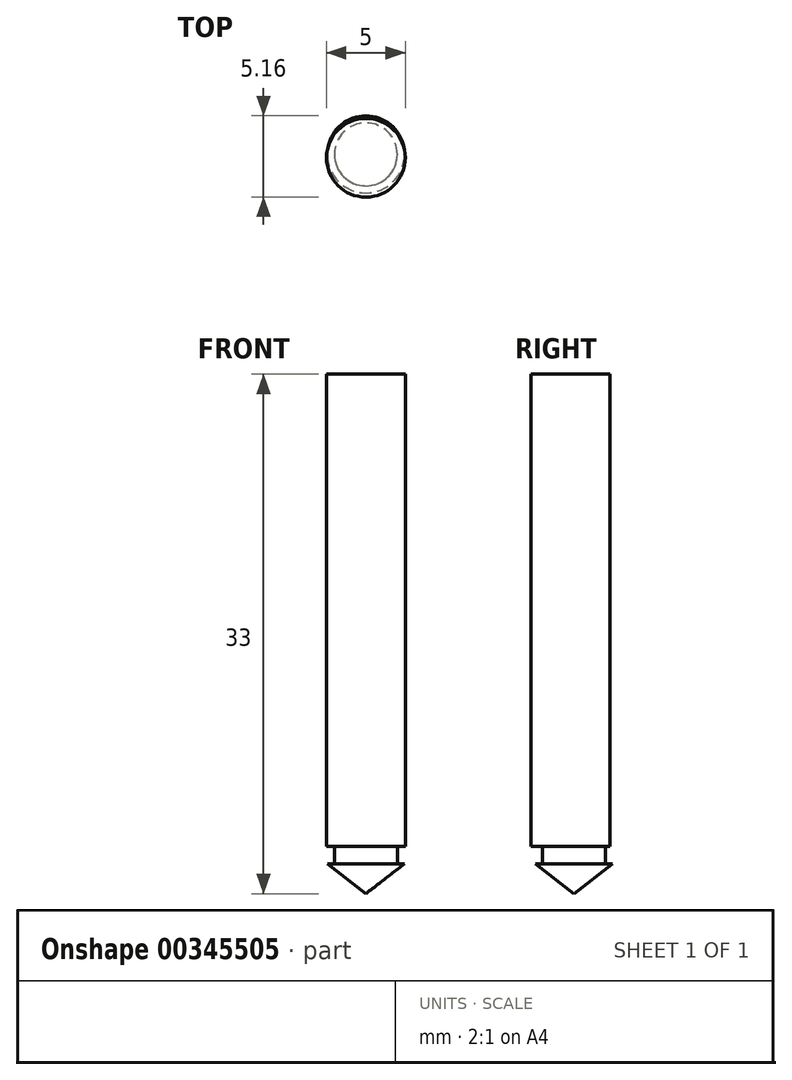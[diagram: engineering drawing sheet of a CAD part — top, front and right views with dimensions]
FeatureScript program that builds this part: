
annotation { "Feature Type Name" : "Feature", "Feature Type Description" : "" }
export const myFeature = defineFeature(function(context is Context, id is Id, definition is map)
    precondition{}
    {
        {
            var Q0;
            Q0=qCreatedBy(makeId("Front.planeOp"),FACE);
            var sketch = newSketch(context, id + "F0", { "sketchPlane" : qUnion([Q0])});
            skLineSegment(sketch, "E0", {"start": v(0, 0) * mm, "end": v(0, 1.9) * mm});
            skLineSegment(sketch, "E1", {"start": v(0, 1.9) * mm, "end": v(2.45, 1.9) * mm});
            skLineSegment(sketch, "E2", {"start": v(2.45, 1.9) * mm, "end": v(0, 0) * mm});
            skSolve(sketch);
        }
        {
            var Q0;
            Q0 = qSketchRegion(id + "F0", true);
            var Q1;
            Q1=sQuery(id+"F0.wireOp",EDGE,"E0");
            revolve(context, id + "F1", {"entities" : qUnion([Q0]), "axis" : qUnion([Q1]), "revolveType" : RevolveType.FULL});
        }
        {
            var Q0;
            Q0=makeQuery(id+"F1.opRevolve","SWEPT_FACE",FACE,{"disambiguationData":[OSD([sQuery(id+"F0.wireOp",EDGE,"E1")])]});
            var sketch = newSketch(context, id + "F2", { "sketchPlane" : qUnion([Q0])});
            skCircle(sketch, "E3", {"center": v(0, 0) * mm, "radius": 2 * mm});
            skSolve(sketch);
        }
        {
            var Q0;
            Q0 = qSketchRegion(id + "F2", true);
            extrude(context, id + "F3", {"entities" : qUnion([Q0]), "operationType" : NewBodyOperationType.ADD, "depth" : 1.1 * mm});
        }
        {
            var Q0;
            Q0=makeQuery(id+"F3.opExtrude","CAP_FACE",FACE,{"disambiguationData":[OSD([sQuery(id+"F2.wireOp",EDGE,"E3")])],"isStart":false});
            var sketch = newSketch(context, id + "F4", { "sketchPlane" : qUnion([Q0])});
            skCircle(sketch, "E4", {"center": v(0, -0.21) * mm, "radius": 2.5 * mm});
            skSolve(sketch);
        }
        {
            var Q0;
            Q0 = qSketchRegion(id + "F4", true);
            extrude(context, id + "F5", {"entities" : qUnion([Q0]), "operationType" : NewBodyOperationType.ADD, "depth" : 30 * mm});
        }
    });
